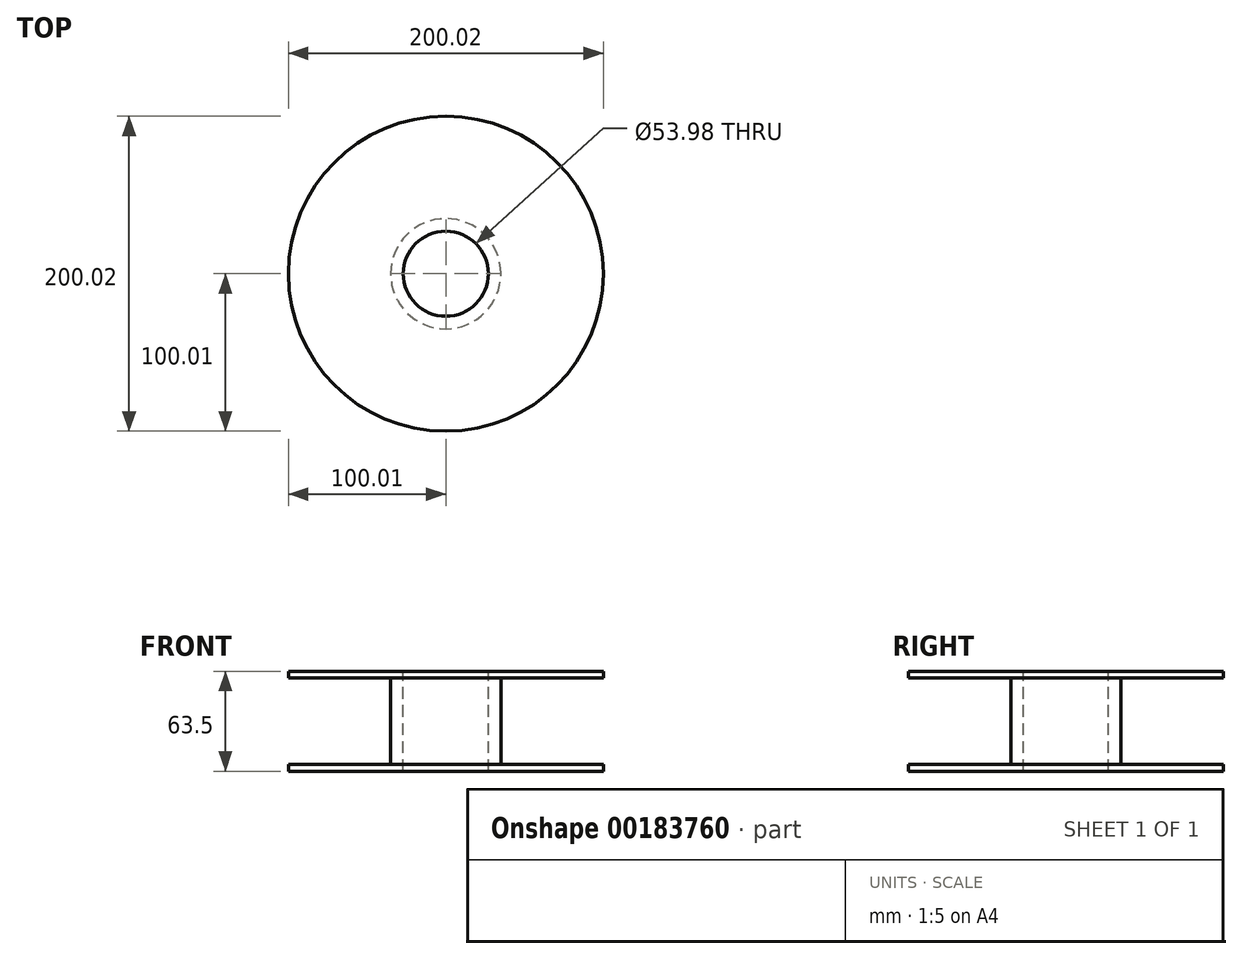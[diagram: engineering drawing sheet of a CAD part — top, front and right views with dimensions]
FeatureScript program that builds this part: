
annotation { "Feature Type Name" : "Feature", "Feature Type Description" : "" }
export const myFeature = defineFeature(function(context is Context, id is Id, definition is map)
    precondition{}
    {
        {
            var Q0;
            Q0=qCreatedBy(makeId("Top.planeOp"),FACE);
            var sketch = newSketch(context, id + "F0", { "sketchPlane" : qUnion([Q0])});
            skCircle(sketch, "E0", {"center": v(0, 0) * mm, "radius": 100.01 * mm});
            skSolve(sketch);
        }
        {
            var Q0;
            Q0=makeQuery(id+"F0.imprint","IMPRINT",FACE,{"disambiguationData":[TD([[makeQuery(id+"F0.imprint","IMPRINT",EDGE,{"derivedFrom":sQuery(id+"F0.wireOp",EDGE,"E0")}),1.0]])]});
            extrude(context, id + "F1", {"entities" : qUnion([Q0]), "endBound" : BoundingType.SYMMETRIC, "depth" : 63.5 * mm});
        }
        {
            var Q0;
            Q0=qCreatedBy(makeId("Top.planeOp"),FACE);
            var sketch = newSketch(context, id + "F2", { "sketchPlane" : qUnion([Q0])});
            skCircle(sketch, "E1", {"center": v(0, 0) * mm, "radius": 35 * mm});
            skCircle(sketch, "E2", {"center": v(0, 0) * mm, "radius": 125 * mm});
            skSolve(sketch);
        }
        {
            var Q0;
            Q0 = qSketchRegion(id + "F2", true);
            extrude(context, id + "F3", {"entities" : qUnion([Q0]), "operationType" : NewBodyOperationType.REMOVE, "endBound" : BoundingType.SYMMETRIC, "oppositeDirection" : true, "depth" : 55 * mm});
        }
        {
            var Q0;
            Q0=qCreatedBy(makeId("Top.planeOp"),FACE);
            var sketch = newSketch(context, id + "F4", { "sketchPlane" : qUnion([Q0])});
            skCircle(sketch, "E3", {"center": v(0, 0) * mm, "radius": 26.99 * mm});
            skSolve(sketch);
        }
        {
            var Q0;
            Q0 = qSketchRegion(id + "F4", true);
            extrude(context, id + "F5", {"entities" : qUnion([Q0]), "operationType" : NewBodyOperationType.REMOVE, "endBound" : BoundingType.THROUGH_ALL, "oppositeDirection" : true, "depth" : 25 * mm, "hasSecondDirection" : true, "secondDirectionBound" : SecondDirectionBoundingType.THROUGH_ALL, "secondDirectionOppositeDirection" : false, "secondDirectionDepth" : 25 * mm});
        }
    });
